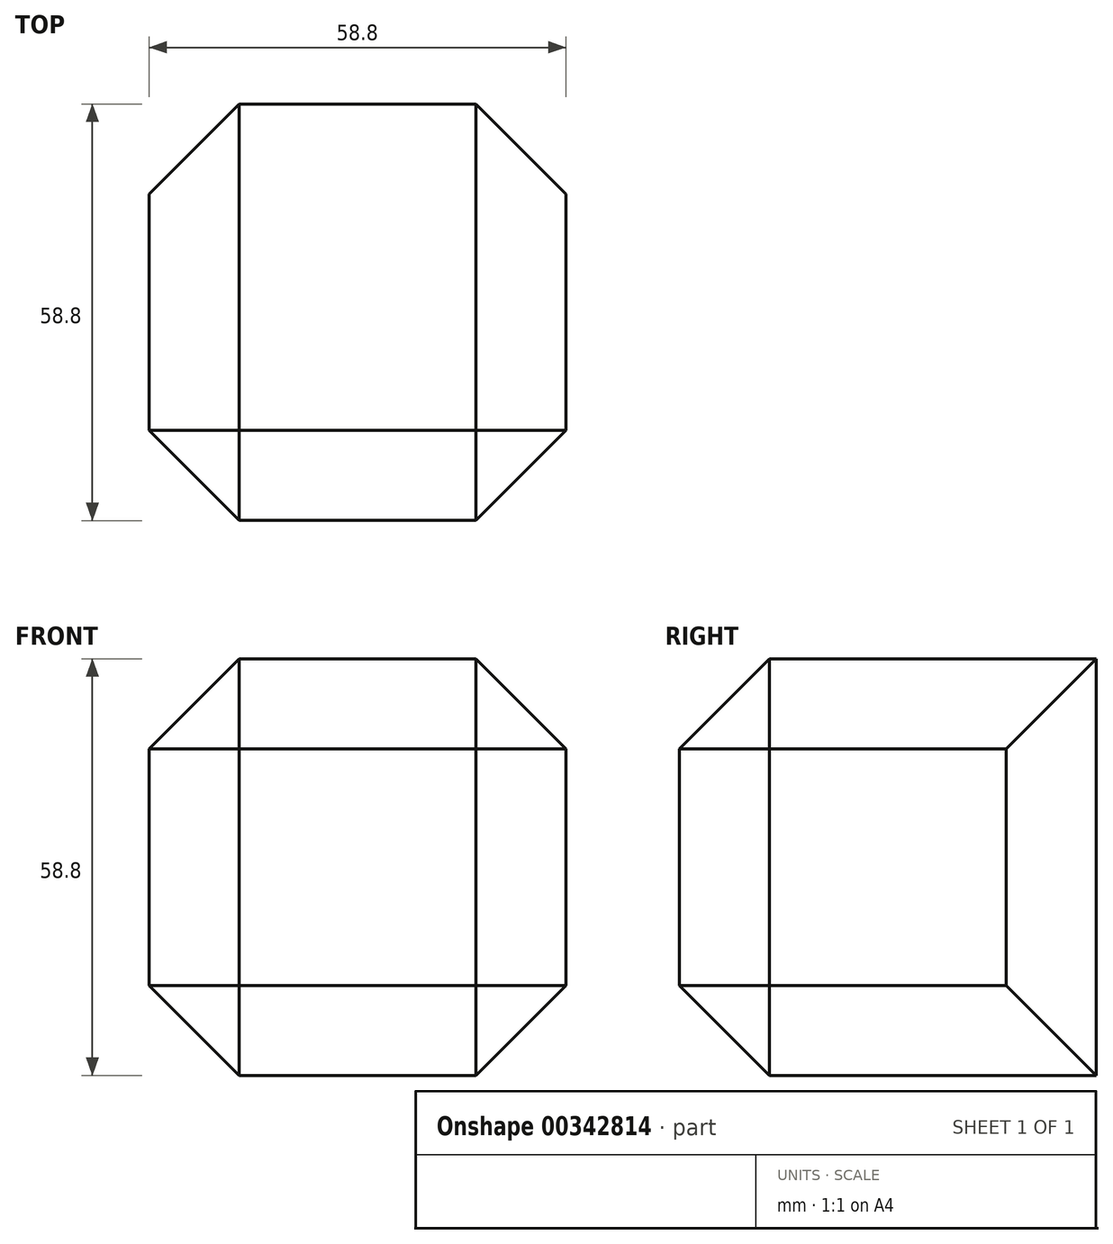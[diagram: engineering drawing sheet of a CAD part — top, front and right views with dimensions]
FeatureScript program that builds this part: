
annotation { "Feature Type Name" : "Feature", "Feature Type Description" : "" }
export const myFeature = defineFeature(function(context is Context, id is Id, definition is map)
    precondition{}
    {
        {
            var Q0;
            Q0=qCreatedBy(makeId("Top.planeOp"),FACE);
            var sketch = newSketch(context, id + "F0", { "sketchPlane" : qUnion([Q0])});
            skLineSegment(sketch, "E0.bottom", {"start": v(29.4, -29.4) * mm, "end": v(-29.4, -29.4) * mm});
            skLineSegment(sketch, "E0.top", {"start": v(29.4, 29.4) * mm, "end": v(-29.4, 29.4) * mm});
            skLineSegment(sketch, "E0.left", {"start": v(29.4, -29.4) * mm, "end": v(29.4, 29.4) * mm});
            skLineSegment(sketch, "E0.right", {"start": v(-29.4, -29.4) * mm, "end": v(-29.4, 29.4) * mm});
            skPoint(sketch, "E0.middle", {"position": v(0, 0) * mm});
            skSolve(sketch);
        }
        {
            var Q0;
            Q0=makeQuery(id+"F0.imprint","IMPRINT",FACE,{"disambiguationData":[TD([[makeQuery(id+"F0.imprint","IMPRINT",EDGE,{"derivedFrom":sQuery(id+"F0.wireOp",EDGE,"E0.bottom")}),-1.0]])]});
            extrude(context, id + "F1", {"entities" : qUnion([Q0]), "endBound" : BoundingType.SYMMETRIC, "depth" : 25.4 * mm});
        }
        {
            var Q0;
            Q0=makeQuery(id+"F1.opExtrude","SWEPT_FACE",FACE,{"disambiguationData":[OSD([sQuery(id+"F0.wireOp",EDGE,"E0.bottom")])]});
            var sketch = newSketch(context, id + "F2", { "sketchPlane" : qUnion([Q0])});
            skLineSegment(sketch, "E1.bottom", {"start": v(29.4, -29.4) * mm, "end": v(-29.4, -29.4) * mm});
            skLineSegment(sketch, "E1.top", {"start": v(29.4, 29.4) * mm, "end": v(-29.4, 29.4) * mm});
            skLineSegment(sketch, "E1.left", {"start": v(29.4, -29.4) * mm, "end": v(29.4, 29.4) * mm});
            skLineSegment(sketch, "E1.right", {"start": v(-29.4, -29.4) * mm, "end": v(-29.4, 29.4) * mm});
            skPoint(sketch, "E1.middle", {"position": v(0, 0) * mm});
            skSolve(sketch);
        }
        {
            var Q0;
            {var subQ0=sQuery(id+"F2.wireOp",EDGE,"E1.top");Q0=makeQuery(id+"F2.imprint","IMPRINT",FACE,{"disambiguationData":[TD([[makeQuery(id+"F2.imprint","IMPRINT",EDGE,{"derivedFrom":subQ0}),1.0]])]});}
            var Q1;
            {var subQ0=sQuery(id+"F2.wireOp",EDGE,"E1.bottom");Q1=makeQuery(id+"F2.imprint","IMPRINT",FACE,{"disambiguationData":[TD([[makeQuery(id+"F2.imprint","IMPRINT",EDGE,{"derivedFrom":subQ0}),-1.0]])]});}
            var Q2;
            {var subQ1=sQuery(id+"F0.wireOp",EDGE,"E0.bottom");var subQ2=makeQuery(id+"F1.opExtrude","CAP_EDGE",EDGE,{"disambiguationData":[OSD([subQ1])],"isStart":true});Q2=makeQuery(id+"F2.imprint","IMPRINT",FACE,{"disambiguationData":[TD([[makeQuery(id+"F2.imprint","IMPRINT",EDGE,{"derivedFrom":subQ2}),-1.0]])]});}
            var Q3;
            Q3=makeQuery(id+"F1.opExtrude","SWEPT_FACE",FACE,{"disambiguationData":[OSD([sQuery(id+"F0.wireOp",EDGE,"E0.top")])]});
            extrude(context, id + "F3", {"entities" : qUnion([Q0, Q1, Q2]), "operationType" : NewBodyOperationType.ADD, "endBound" : BoundingType.UP_TO_SURFACE, "oppositeDirection" : true, "endBoundEntityFace" : qUnion([Q3]), "depth" : 25.4 * mm});
        }
        {
            var Q0;
            Q0=makeQuery(id+"F3.opExtrude","TWEAK_EDGE",EDGE,{"derivedFrom":[makeQuery(id+"F1.opExtrude","SWEPT_FACE",FACE,{"disambiguationData":[OSD([sQuery(id+"F0.wireOp",EDGE,"E0.top")])]}),makeQuery(id+"F2.imprint","IMPRINT",EDGE,{"derivedFrom":sQuery(id+"F2.wireOp",EDGE,"E1.top")})]});
            var Q1;
            Q1=makeQuery(id+"F3.opExtrude","SWEPT_EDGE",EDGE,{"disambiguationData":[OSD([sQuery(id+"F2.wireOp",EDGE,"E1.top"),sQuery(id+"F2.wireOp",EDGE,"E1.right")])]});
            var Q2;
            {var subQ0=sQuery(id+"F2.wireOp",EDGE,"E1.right");var subQ1=sQuery(id+"F0.wireOp",EDGE,"E0.bottom");var subQ2=makeQuery(id+"F2.imprint","INTERSECT",VERTEX,{"derivedFrom":[makeQuery(id+"F1.opExtrude","CAP_EDGE",EDGE,{"disambiguationData":[OSD([subQ1])],"isStart":false}),subQ0]});var subQ3=makeQuery(id+"F2.imprint","INTERSECT",VERTEX,{"derivedFrom":[makeQuery(id+"F1.opExtrude","CAP_EDGE",EDGE,{"disambiguationData":[OSD([subQ1])],"isStart":true}),subQ0]});var subQ4=sQuery(id+"F0.wireOp",EDGE,"E0.top");Q2=makeQuery(id+"F3.boolean.opBoolean","MERGE",EDGE,{"derivedFrom":[makeQuery(id+"F1.opExtrude","SWEPT_EDGE",EDGE,{"disambiguationData":[OSD([subQ4,sQuery(id+"F0.wireOp",EDGE,"E0.right")])]}),makeQuery(id+"F3.opExtrude","TWEAK_EDGE",EDGE,{"derivedFrom":[makeQuery(id+"F1.opExtrude","SWEPT_FACE",FACE,{"disambiguationData":[OSD([subQ4])]}),makeQuery(id+"F2.imprint","IMPRINT",EDGE,{"disambiguationData":[TD([[subQ3,1.0],[makeQuery(id+"F2.imprint","INTERSECT",VERTEX,{"derivedFrom":[sQuery(id+"F2.wireOp",EDGE,"E1.bottom"),subQ0]}),-1.0]])],"derivedFrom":subQ0}),makeQuery(id+"F2.imprint","IMPRINT",EDGE,{"disambiguationData":[TD([[subQ3,1.0],[subQ2,-1.0]])],"derivedFrom":subQ0}),makeQuery(id+"F2.imprint","IMPRINT",EDGE,{"disambiguationData":[TD([[subQ2,-1.0],[makeQuery(id+"F2.imprint","INTERSECT",VERTEX,{"derivedFrom":[sQuery(id+"F2.wireOp",EDGE,"E1.top"),subQ0]}),1.0]])],"derivedFrom":subQ0})]})]});}
            var Q3;
            Q3=makeQuery(id+"F3.opExtrude","SWEPT_EDGE",EDGE,{"disambiguationData":[OSD([sQuery(id+"F2.wireOp",EDGE,"E1.top"),sQuery(id+"F2.wireOp",EDGE,"E1.left")])]});
            var Q4;
            Q4=makeQuery(id+"F3.opExtrude","CAP_EDGE",EDGE,{"disambiguationData":[OSD([sQuery(id+"F2.wireOp",EDGE,"E1.top")])],"isStart":true});
            var Q5;
            Q5=makeQuery(id+"F3.opExtrude","TWEAK_EDGE",EDGE,{"derivedFrom":[makeQuery(id+"F1.opExtrude","SWEPT_FACE",FACE,{"disambiguationData":[OSD([sQuery(id+"F0.wireOp",EDGE,"E0.top")])]}),makeQuery(id+"F2.imprint","IMPRINT",EDGE,{"derivedFrom":sQuery(id+"F2.wireOp",EDGE,"E1.bottom")})]});
            var Q6;
            {var subQ0=sQuery(id+"F2.wireOp",EDGE,"E1.left");var subQ1=sQuery(id+"F0.wireOp",EDGE,"E0.bottom");var subQ2=makeQuery(id+"F2.imprint","INTERSECT",VERTEX,{"derivedFrom":[makeQuery(id+"F1.opExtrude","CAP_EDGE",EDGE,{"disambiguationData":[OSD([subQ1])],"isStart":false}),subQ0]});var subQ3=makeQuery(id+"F2.imprint","INTERSECT",VERTEX,{"derivedFrom":[makeQuery(id+"F1.opExtrude","CAP_EDGE",EDGE,{"disambiguationData":[OSD([subQ1])],"isStart":true}),subQ0]});var subQ4=sQuery(id+"F0.wireOp",EDGE,"E0.top");Q6=makeQuery(id+"F3.boolean.opBoolean","MERGE",EDGE,{"derivedFrom":[makeQuery(id+"F1.opExtrude","SWEPT_EDGE",EDGE,{"disambiguationData":[OSD([subQ4,sQuery(id+"F0.wireOp",EDGE,"E0.left")])]}),makeQuery(id+"F3.opExtrude","TWEAK_EDGE",EDGE,{"derivedFrom":[makeQuery(id+"F1.opExtrude","SWEPT_FACE",FACE,{"disambiguationData":[OSD([subQ4])]}),makeQuery(id+"F2.imprint","IMPRINT",EDGE,{"disambiguationData":[TD([[subQ3,1.0],[makeQuery(id+"F2.imprint","INTERSECT",VERTEX,{"derivedFrom":[sQuery(id+"F2.wireOp",EDGE,"E1.bottom"),subQ0]}),-1.0]])],"derivedFrom":subQ0}),makeQuery(id+"F2.imprint","IMPRINT",EDGE,{"disambiguationData":[TD([[subQ3,1.0],[subQ2,-1.0]])],"derivedFrom":subQ0}),makeQuery(id+"F2.imprint","IMPRINT",EDGE,{"disambiguationData":[TD([[subQ2,-1.0],[makeQuery(id+"F2.imprint","INTERSECT",VERTEX,{"derivedFrom":[sQuery(id+"F2.wireOp",EDGE,"E1.top"),subQ0]}),1.0]])],"derivedFrom":subQ0})]})]});}
            var Q7;
            Q7=makeQuery(id+"F3.boolean.opBoolean","MERGE",EDGE,{"derivedFrom":[makeQuery(id+"F1.opExtrude","SWEPT_EDGE",EDGE,{"disambiguationData":[OSD([sQuery(id+"F0.wireOp",EDGE,"E0.bottom"),sQuery(id+"F0.wireOp",EDGE,"E0.right")])]}),makeQuery(id+"F3.opExtrude","CAP_EDGE",EDGE,{"disambiguationData":[OSD([sQuery(id+"F2.wireOp",EDGE,"E1.right")])],"isStart":true})]});
            var Q8;
            Q8=makeQuery(id+"F3.opExtrude","SWEPT_EDGE",EDGE,{"disambiguationData":[OSD([sQuery(id+"F2.wireOp",EDGE,"E1.bottom"),sQuery(id+"F2.wireOp",EDGE,"E1.right")])]});
            var Q9;
            Q9=makeQuery(id+"F3.opExtrude","CAP_EDGE",EDGE,{"disambiguationData":[OSD([sQuery(id+"F2.wireOp",EDGE,"E1.bottom")])],"isStart":true});
            var Q10;
            Q10=makeQuery(id+"F3.boolean.opBoolean","MERGE",EDGE,{"derivedFrom":[makeQuery(id+"F1.opExtrude","SWEPT_EDGE",EDGE,{"disambiguationData":[OSD([sQuery(id+"F0.wireOp",EDGE,"E0.bottom"),sQuery(id+"F0.wireOp",EDGE,"E0.left")])]}),makeQuery(id+"F3.opExtrude","CAP_EDGE",EDGE,{"disambiguationData":[OSD([sQuery(id+"F2.wireOp",EDGE,"E1.left")])],"isStart":true})]});
            var Q11;
            Q11=makeQuery(id+"F3.opExtrude","SWEPT_EDGE",EDGE,{"disambiguationData":[OSD([sQuery(id+"F2.wireOp",EDGE,"E1.bottom"),sQuery(id+"F2.wireOp",EDGE,"E1.left")])]});
            chamfer(context, id + "F4", {"entities" : qUnion([Q0, Q1, Q2, Q3, Q4, Q5, Q6, Q7, Q8, Q9, Q10, Q11]), "width" : 12.7 * mm, "tangentPropagation" : true});
        }
    });
